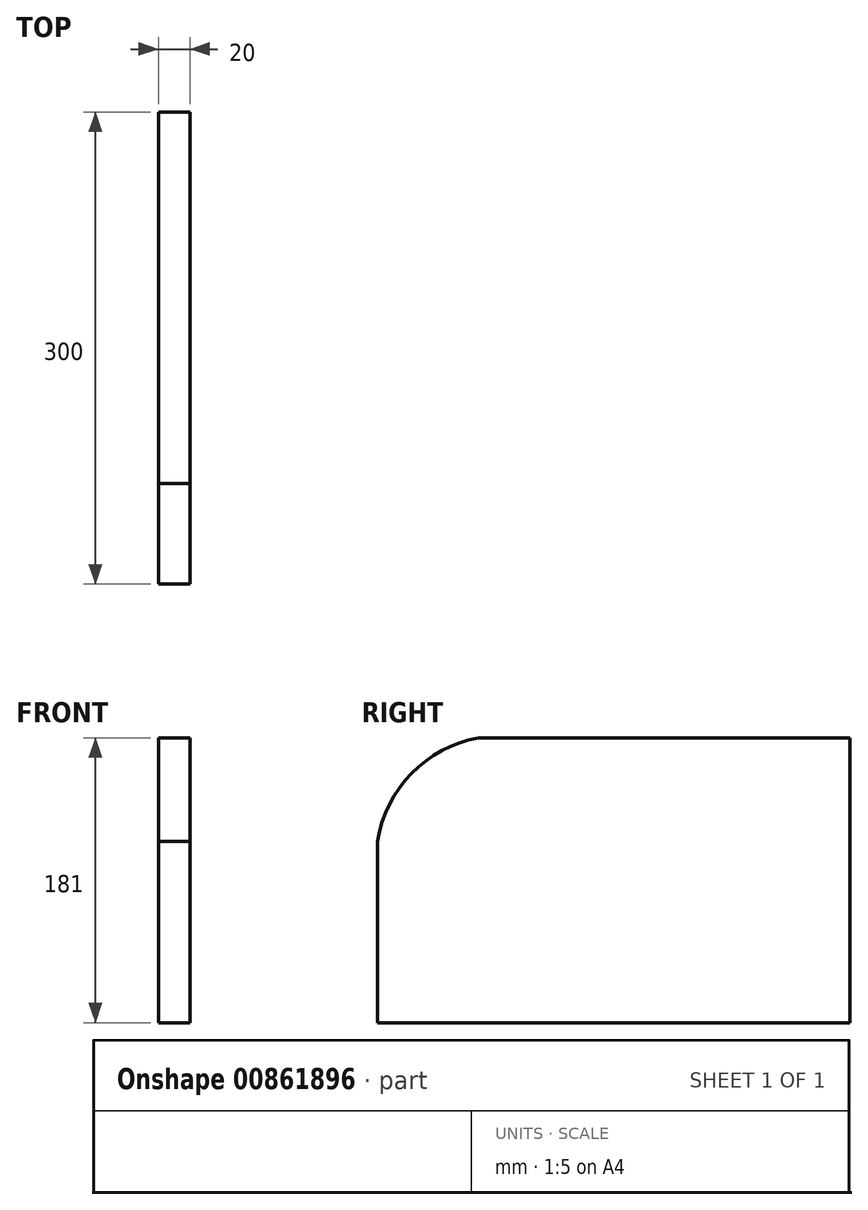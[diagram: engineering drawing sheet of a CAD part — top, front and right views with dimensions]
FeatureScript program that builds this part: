
annotation { "Feature Type Name" : "Feature", "Feature Type Description" : "" }
export const myFeature = defineFeature(function(context is Context, id is Id, definition is map)
    precondition{}
    {
        {
            var Q0;
            Q0=qCreatedBy(makeId("Right.planeOp"),FACE);
            var sketch = newSketch(context, id + "F0", { "sketchPlane" : qUnion([Q0])});
            skLineSegment(sketch, "E0.bottom", {"start": v(206.97, 137.53) * mm, "end": v(-93.03, 137.53) * mm});
            skLineSegment(sketch, "E0.top", {"start": v(206.97, -43.47) * mm, "end": v(-93.03, -43.47) * mm});
            skLineSegment(sketch, "E0.left", {"start": v(206.97, 137.53) * mm, "end": v(206.97, -43.47) * mm});
            skLineSegment(sketch, "E0.right", {"start": v(-93.03, 137.53) * mm, "end": v(-93.03, -43.47) * mm});
            skSolve(sketch);
        }
        {
            var Q0;
            Q0=makeQuery(id+"F0.imprint","IMPRINT",FACE,{"disambiguationData":[TD([[makeQuery(id+"F0.imprint","IMPRINT",EDGE,{"derivedFrom":sQuery(id+"F0.wireOp",EDGE,"E0.bottom")}),1.0]])]});
            extrude(context, id + "F1", {"entities" : qUnion([Q0]), "depth" : 20 * mm, "offsetDistance" : 25 * mm});
        }
        {
            var Q0;
            Q0=makeQuery(id+"F1.opExtrude","CAP_FACE",FACE,{"disambiguationData":[OSD([sQuery(id+"F0.wireOp",EDGE,"E0.bottom"),sQuery(id+"F0.wireOp",EDGE,"E0.top"),sQuery(id+"F0.wireOp",EDGE,"E0.left"),sQuery(id+"F0.wireOp",EDGE,"E0.right")])],"isStart":true});
            var sketch = newSketch(context, id + "F2", { "sketchPlane" : qUnion([Q0])});
            skArc(sketch, "E1", {"start": v(93.03, 47.03) * mm, "mid": v(69.95, 116.37) * mm, "end": v(0, 137.53) * mm});
            skSolve(sketch);
        }
        {
            var Q0;
            {var subQ0=sQuery(id+"F2.wireOp",EDGE,"E1");var subQ1=makeQuery(id+"F1.opExtrude","CAP_EDGE",EDGE,{"disambiguationData":[OSD([sQuery(id+"F0.wireOp",EDGE,"E0.right")])],"isStart":true});var subQ2=makeQuery(id+"F2.imprint","INTERSECT",VERTEX,{"disambiguationData":[OD(1.0)],"derivedFrom":[subQ1,subQ0]});Q0=makeQuery(id+"F2.imprint","IMPRINT",FACE,{"disambiguationData":[TD([[makeQuery(id+"F2.imprint","IMPRINT",EDGE,{"disambiguationData":[TD([[subQ2,-1.0]])],"derivedFrom":subQ0}),-1.0]])]});}
            extrude(context, id + "F3", {"entities" : qUnion([Q0]), "operationType" : NewBodyOperationType.REMOVE, "oppositeDirection" : true, "depth" : 25 * mm, "offsetDistance" : 25 * mm});
        }
    });
